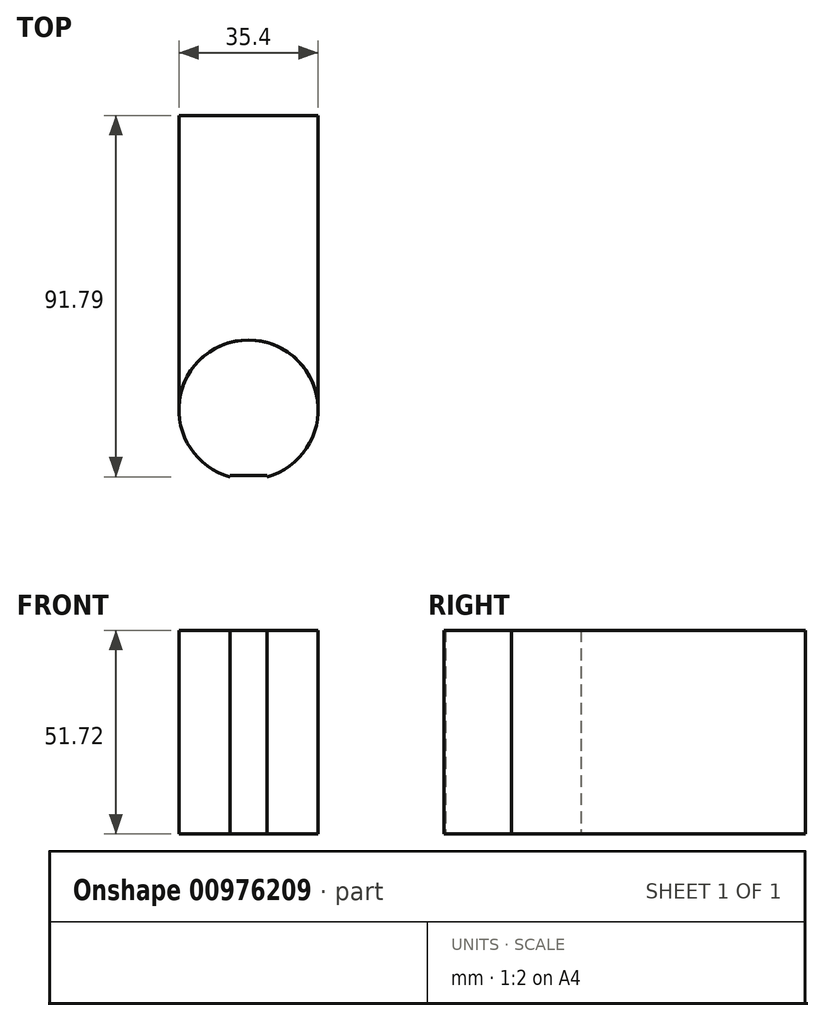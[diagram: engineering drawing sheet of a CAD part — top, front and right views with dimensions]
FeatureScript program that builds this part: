
annotation { "Feature Type Name" : "Feature", "Feature Type Description" : "" }
export const myFeature = defineFeature(function(context is Context, id is Id, definition is map)
    precondition{}
    {
        {
            var Q0;
            Q0=qCreatedBy(makeId("Top.planeOp"),FACE);
            var sketch = newSketch(context, id + "F0", { "sketchPlane" : qUnion([Q0])});
            skLineSegment(sketch, "E0.bottom", {"start": v(17.7, 37.36) * mm, "end": v(-17.7, 37.36) * mm});
            skLineSegment(sketch, "E0.top", {"start": v(17.7, -37.36) * mm, "end": v(-17.7, -37.36) * mm});
            skLineSegment(sketch, "E0.left", {"start": v(17.7, 37.36) * mm, "end": v(17.7, -37.36) * mm});
            skLineSegment(sketch, "E0.right", {"start": v(-17.7, 37.36) * mm, "end": v(-17.7, -37.36) * mm});
            skPoint(sketch, "E0.middle", {"position": v(0, 0) * mm});
            skCircle(sketch, "E1", {"center": v(0, -37.36) * mm, "radius": 17.7 * mm});
            skLineSegment(sketch, "E2.bottom", {"start": v(-4.67, -54.09) * mm, "end": v(4.67, -54.09) * mm});
            skLineSegment(sketch, "E2.top", {"start": v(-4.67, -56.04) * mm, "end": v(4.67, -56.04) * mm});
            skLineSegment(sketch, "E2.left", {"start": v(4.67, -56.04) * mm, "end": v(4.67, -54.09) * mm});
            skLineSegment(sketch, "E2.right", {"start": v(-4.67, -56.04) * mm, "end": v(-4.67, -54.09) * mm});
            skPoint(sketch, "E2.middle", {"position": v(0, -55.06) * mm});
            skSolve(sketch);
        }
        {
            var Q0;
            Q0=makeQuery(id+"F0.imprint","IMPRINT",FACE,{"disambiguationData":[TD([[makeQuery(id+"F0.imprint","IMPRINT",EDGE,{"derivedFrom":sQuery(id+"F0.wireOp",EDGE,"E0.bottom")}),1.0]])]});
            var sketch = newSketch(context, id + "F1", { "sketchPlane" : qUnion([Q0])});
            skSolve(sketch);
        }
        {
            var Q0;
            {var subQ0=sQuery(id+"F0.wireOp",EDGE,"E0.top");Q0=makeQuery(id+"F0.imprint","IMPRINT",FACE,{"disambiguationData":[TD([[makeQuery(id+"F0.imprint","IMPRINT",EDGE,{"derivedFrom":subQ0}),-1.0]])]});}
            var Q1;
            {var subQ2=sQuery(id+"F0.wireOp",EDGE,"E0.top");Q1=makeQuery(id+"F0.imprint","IMPRINT",FACE,{"disambiguationData":[TD([[makeQuery(id+"F0.imprint","IMPRINT",EDGE,{"derivedFrom":subQ2}),1.0]])]});}
            var Q2;
            Q2=makeQuery(id+"F1.imprint","IMPRINT",FACE,{"disambiguationData":[TD([[makeQuery(id+"F1.imprint","IMPRINT",EDGE,{"derivedFrom":makeQuery(id+"F0.imprint","IMPRINT",EDGE,{"derivedFrom":sQuery(id+"F0.wireOp",EDGE,"E0.bottom")})}),1.0]])]});
            extrude(context, id + "F2", {"entities" : qUnion([Q0, Q1, Q2]), "depth" : 51.72 * mm, "offsetDistance" : 25.4 * mm});
        }
    });
